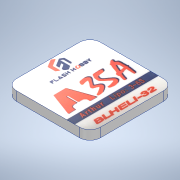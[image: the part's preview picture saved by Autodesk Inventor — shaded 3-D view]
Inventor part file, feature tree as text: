
AUTODESK INVENTOR PART (.ipt)
format: ipt  version: 2022 (Build 260153000, 153)  size: 1,058,304 bytes
history: native  units: in
note: dims shown in document units (in); Inventor stores cm internally (conversion verified against a paired STEP export)
features: other x2, sketch x2, extrude x1, fillet x1
ambient origin geometry x8: Origin, YZ Plane, XZ Plane, XY Plane, X Axis, Y Axis, Z Axis, Center Point
bodies: Solid1 (feature_tree)
feature tree (6):
  extrude  "Extrusion1"  Depth=0.6299in
  fillet  "Fillet1"  Radius=0.0689in
  other  "Decal1"
  sketch  "Sketch1"  dims[d0=0.6299in d1=0.6299in d2=0.0689in d3=0.0in]
  sketch  "Sketch2"  dims[d4=0.0787in]
  other  "Image1"
